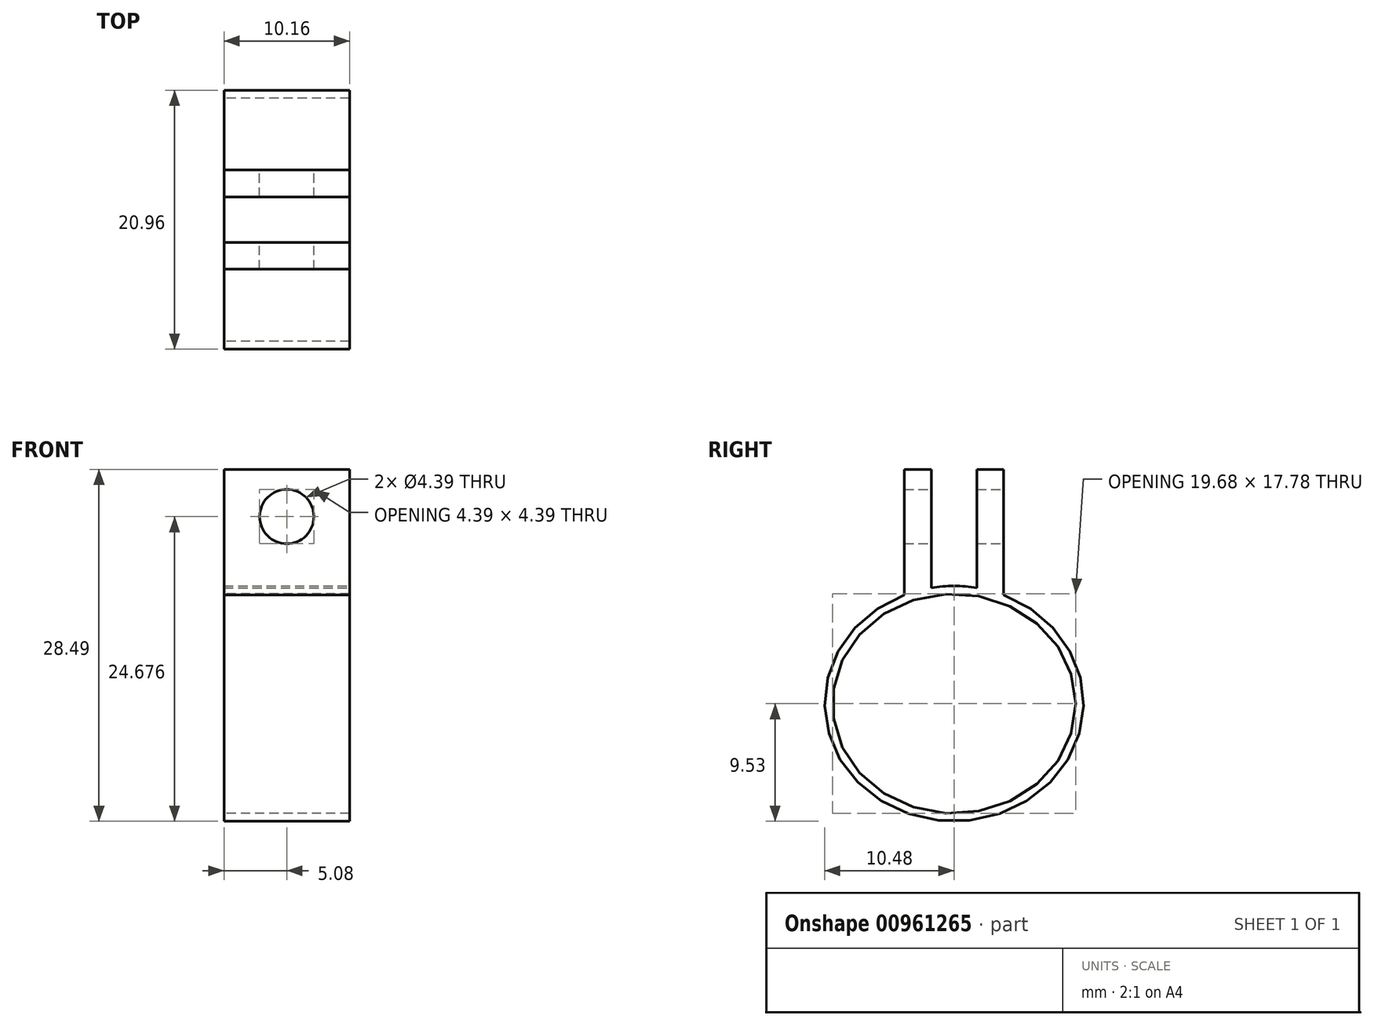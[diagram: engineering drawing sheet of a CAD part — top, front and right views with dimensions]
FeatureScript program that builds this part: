
annotation { "Feature Type Name" : "Feature", "Feature Type Description" : "" }
export const myFeature = defineFeature(function(context is Context, id is Id, definition is map)
    precondition{}
    {
        {
            var Q0;
            Q0=qCreatedBy(makeId("Right.planeOp"),FACE);
            var sketch = newSketch(context, id + "F0", { "sketchPlane" : qUnion([Q0])});
            skEllipse(sketch, "E0", {"center": v(0, 0) * mm, "majorRadius": 9.84 * mm, "minorRadius": 8.9 * mm, "majorAxis": v(1, 0)});
            skEllipse(sketch, "E1", {"center": v(0, 0) * mm, "majorRadius": 10.48 * mm, "minorRadius": 9.53 * mm, "majorAxis": v(1, 0)});
            skSolve(sketch);
        }
        {
            var Q0;
            Q0=makeQuery(id+"F0.imprint","IMPRINT",FACE,{"disambiguationData":[TD([[makeQuery(id+"F0.imprint","IMPRINT",EDGE,{"derivedFrom":sQuery(id+"F0.wireOp",EDGE,"E0")}),-1.0]])]});
            extrude(context, id + "F1", {"entities" : qUnion([Q0]), "depth" : 10.16 * mm, "offsetDistance" : 25.4 * mm});
        }
        {
            var Q0;
            Q0=makeQuery(id+"F1.opExtrude","CAP_FACE",FACE,{"disambiguationData":[OSD([sQuery(id+"F0.wireOp",EDGE,"E0"),sQuery(id+"F0.wireOp",EDGE,"E1")])],"isStart":false});
            var sketch = newSketch(context, id + "F2", { "sketchPlane" : qUnion([Q0])});
            skLineSegment(sketch, "E2", {"start": v(-4.02, 8.8) * mm, "end": v(-4.02, 18.96) * mm});
            skLineSegment(sketch, "E3", {"start": v(-4.02, 18.96) * mm, "end": v(-1.85, 18.96) * mm});
            skLineSegment(sketch, "E4", {"start": v(-1.85, 18.96) * mm, "end": v(-1.85, 9.38) * mm});
            skLineSegment(sketch, "E5", {"start": v(0, 7.97) * mm, "end": v(0, 12.7) * mm, "construction": true});
            skLineSegment(sketch, "E6.MirrorCS", {"start": v(1.85, 18.96) * mm, "end": v(1.85, 9.38) * mm});
            skLineSegment(sketch, "E7.MirrorCS", {"start": v(4.02, 18.96) * mm, "end": v(1.85, 18.96) * mm});
            skLineSegment(sketch, "E8.MirrorCS", {"start": v(4.02, 8.8) * mm, "end": v(4.02, 18.96) * mm});
            skSolve(sketch);
        }
        {
            var Q0;
            {var subQ0=sQuery(id+"F2.wireOp",EDGE,"E2");Q0=makeQuery(id+"F2.imprint","IMPRINT",FACE,{"disambiguationData":[TD([[makeQuery(id+"F2.imprint","IMPRINT",EDGE,{"derivedFrom":subQ0}),-1.0]])]});}
            var Q1;
            {var subQ0=sQuery(id+"F2.wireOp",EDGE,"E6.MirrorCS");Q1=makeQuery(id+"F2.imprint","IMPRINT",FACE,{"disambiguationData":[TD([[makeQuery(id+"F2.imprint","IMPRINT",EDGE,{"derivedFrom":subQ0}),1.0]])]});}
            extrude(context, id + "F3", {"entities" : qUnion([Q0, Q1]), "operationType" : NewBodyOperationType.ADD, "oppositeDirection" : true, "depth" : 10.16 * mm, "offsetDistance" : 25.4 * mm});
        }
        {
            var Q0;
            Q0=makeQuery(id+"F3.opExtrude","SWEPT_FACE",FACE,{"disambiguationData":[OSD([sQuery(id+"F2.wireOp",EDGE,"E8.MirrorCS")])]});
            var sketch = newSketch(context, id + "F4", { "sketchPlane" : qUnion([Q0])});
            skCircle(sketch, "E9", {"center": v(-5.08, 15.15) * mm, "radius": 2.2 * mm});
            skLineSegment(sketch, "E10", {"start": v(-5.08, 18.96) * mm, "end": v(-5.08, 8.8) * mm, "construction": true});
            skSolve(sketch);
        }
        {
            var Q0;
            Q0=makeQuery(id+"F4.imprint","IMPRINT",FACE,{"disambiguationData":[TD([[makeQuery(id+"F4.imprint","IMPRINT",EDGE,{"derivedFrom":sQuery(id+"F4.wireOp",EDGE,"E9")}),1.0]])]});
            extrude(context, id + "F5", {"entities" : qUnion([Q0]), "operationType" : NewBodyOperationType.REMOVE, "oppositeDirection" : true, "depth" : 25.4 * mm, "offsetDistance" : 25.4 * mm});
        }
    });
